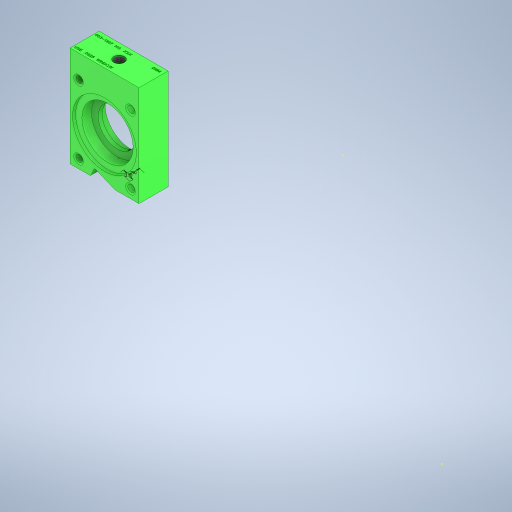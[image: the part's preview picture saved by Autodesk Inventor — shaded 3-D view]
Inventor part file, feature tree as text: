
AUTODESK INVENTOR PART (.ipt)
format: ipt  version: 2024.1 (Build 281209000, 209)  size: 701,440 bytes
history: native  units: in
note: dims shown in document units (in); Inventor stores cm internally (conversion verified against a paired STEP export)
features: hole x6, extrude x4, sketch x3, fillet x1
ambient origin geometry x8: Origin, YZ Plane, XZ Plane, XY Plane, X Axis, Y Axis, Z Axis, Center Point
bodies: Solid1 (feature_tree)
feature tree (14):
  extrude  "Extrusion1"  Depth=0.4in TaperAngle=0.0deg
  extrude  "Extrusion2"  Depth=0.0312in
  extrude  "Extrusion3"  Depth=0.0312in
  hole  "Hole1"  [1 undecoded]
  hole  "Hole2"  [1 undecoded]
  extrude  "Extrusion4"  Depth=0.0312in
  hole  "Hole5"  [1 undecoded]
  hole  "Hole6"  [1 undecoded]
  fillet  "Fillet1"  Radius=1.0in
  hole  "Hole3"  [1 undecoded]
  hole  "Hole4"  [1 undecoded]
  sketch  "Sketch1"  dims[d0=0.5in d1=0.0in d2=0.4in d3=0.0in]
  sketch  "Sketch2"  dims[d4=0.6in d5=0.0in]
  sketch  "Sketch5"  dims[d6=0.211in d7=0.25in d8=0.507in d9=0.25in d10=0.5635in d11=0.25in d12=0.0in d13=0.06in d14=0.75in d15=0.507in d16=0.25in d17=0.5635in d18=1.0in d19=0.8108in d20=0.4583in d21=0.29in d22=0.04in d23=0.75in d24=0.507in d25=0.25in d26=0.5635in d27=1.0in d28=0.8108in d29=0.213in d30=0.75in d31=0.507in d32=0.25in d33=0.5635in d34=0.25in d35=0.0in d36=0.75in d38=135.0deg d39=0.4583in d40=112.5deg d41=0.25in d42=1.0in d43=0.0in d44=0.29in d45=0.196in d46=0.211in d47=0.25in d48=0.375in d49=0.25in d50=0.5635in d51=0.25in d52=0.0in d53=0.06in d54=0.75in d55=0.375in d56=0.25in d57=0.5635in d58=0.6in d59=0.8108in d60=0.0312in]
note: 6 required parameter values undecoded (feature->parameter linkage not recoverable at this tier; creation-order binding heuristic only, values carry confidence <= 0.55)
